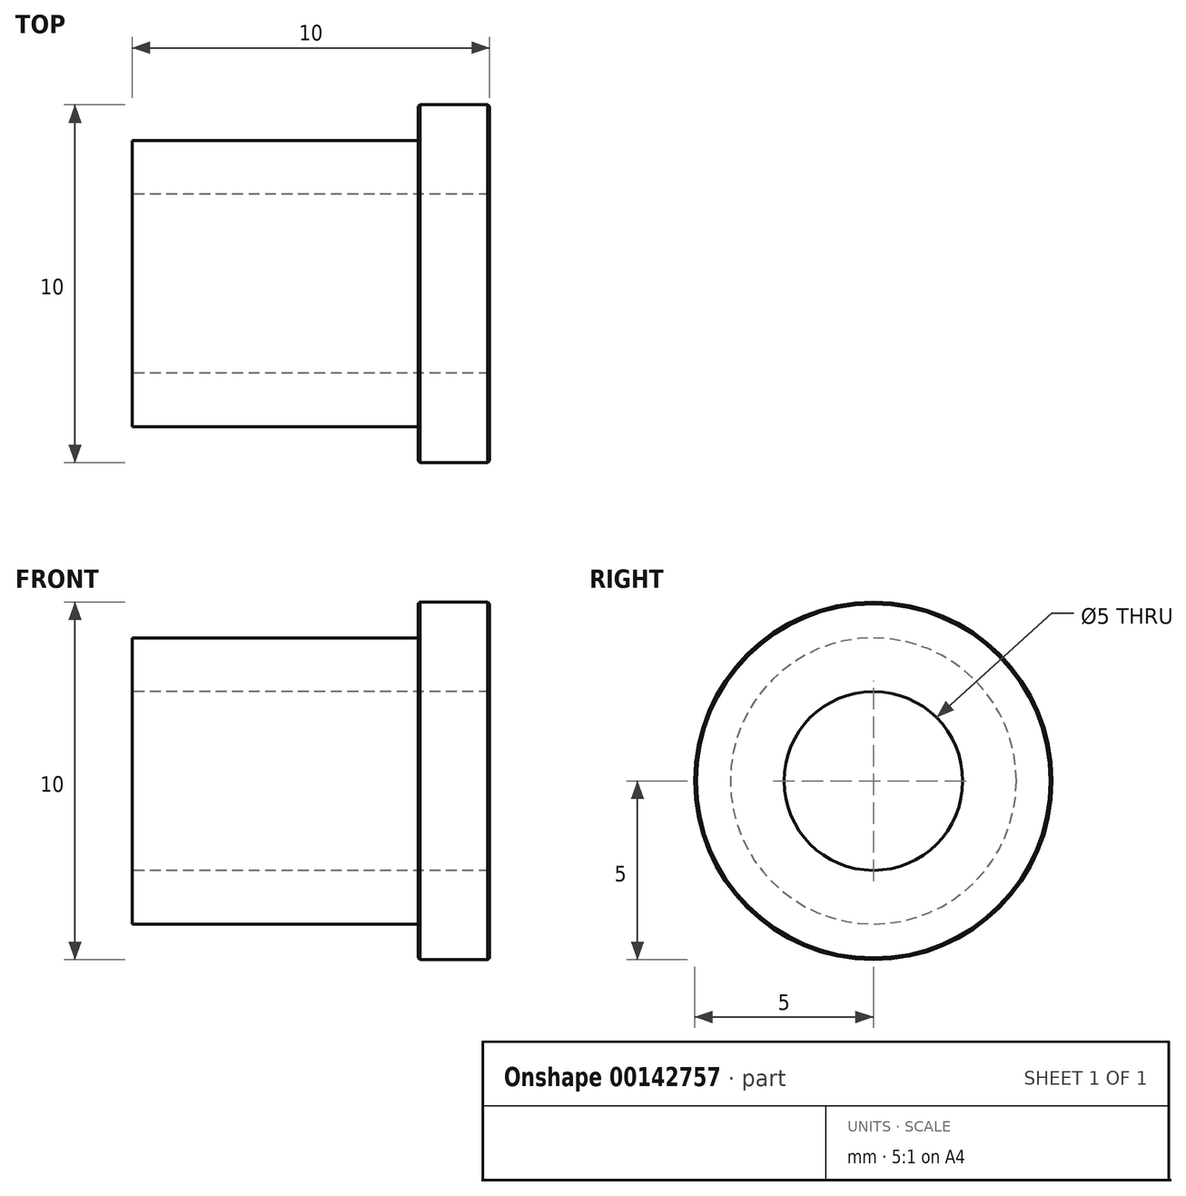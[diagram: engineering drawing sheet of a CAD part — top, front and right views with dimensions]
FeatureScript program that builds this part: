
annotation { "Feature Type Name" : "Feature", "Feature Type Description" : "" }
export const myFeature = defineFeature(function(context is Context, id is Id, definition is map)
    precondition{}
    {
        {
            var Q0;
            Q0=qCreatedBy(makeId("Front.planeOp"),FACE);
            var sketch = newSketch(context, id + "F0", { "sketchPlane" : qUnion([Q0])});
            skLineSegment(sketch, "E0", {"start": v(0, 0) * mm, "end": v(0, 4) * mm});
            skLineSegment(sketch, "E1", {"start": v(0, 4) * mm, "end": v(8, 4) * mm});
            skLineSegment(sketch, "E2", {"start": v(8, 4) * mm, "end": v(8, 5) * mm});
            skLineSegment(sketch, "E3", {"start": v(8, 5) * mm, "end": v(10, 5) * mm});
            skLineSegment(sketch, "E4", {"start": v(10, 5) * mm, "end": v(10, 0) * mm});
            skLineSegment(sketch, "E5", {"start": v(0, 0) * mm, "end": v(10, 0) * mm, "construction": true});
            skLineSegment(sketch, "E6", {"start": v(0, 2.5) * mm, "end": v(10, 2.5) * mm});
            skSolve(sketch);
        }
        {
            var Q0;
            {var subQ1=sQuery(id+"F0.wireOp",EDGE,"E1");Q0=makeQuery(id+"F0.imprint","IMPRINT",FACE,{"disambiguationData":[TD([[makeQuery(id+"F0.imprint","IMPRINT",EDGE,{"derivedFrom":subQ1}),-1.0]])]});}
            var Q1;
            Q1=sQuery(id+"F0.wireOp",EDGE,"E5");
            revolve(context, id + "F1", {"entities" : qUnion([Q0]), "axis" : qUnion([Q1]), "revolveType" : RevolveType.FULL});
        }
        {
            var Q0;
            Q0=makeQuery(id+"F1.opRevolve","SWEPT_EDGE",EDGE,{"disambiguationData":[OSD([sQuery(id+"F0.wireOp",EDGE,"E3"),sQuery(id+"F0.wireOp",EDGE,"E4")])]});
            var Q1;
            Q1=makeQuery(id+"F1.opRevolve","SWEPT_EDGE",EDGE,{"disambiguationData":[OSD([sQuery(id+"F0.wireOp",EDGE,"E2"),sQuery(id+"F0.wireOp",EDGE,"E3")])]});
            chamfer(context, id + "F2", {"entities" : qUnion([Q0, Q1]), "chamferType" : ChamferType.OFFSET_ANGLE, "width" : 0.05 * mm, "oppositeDirection" : false, "angle" : 45 * degree, "tangentPropagation" : true});
        }
    });
